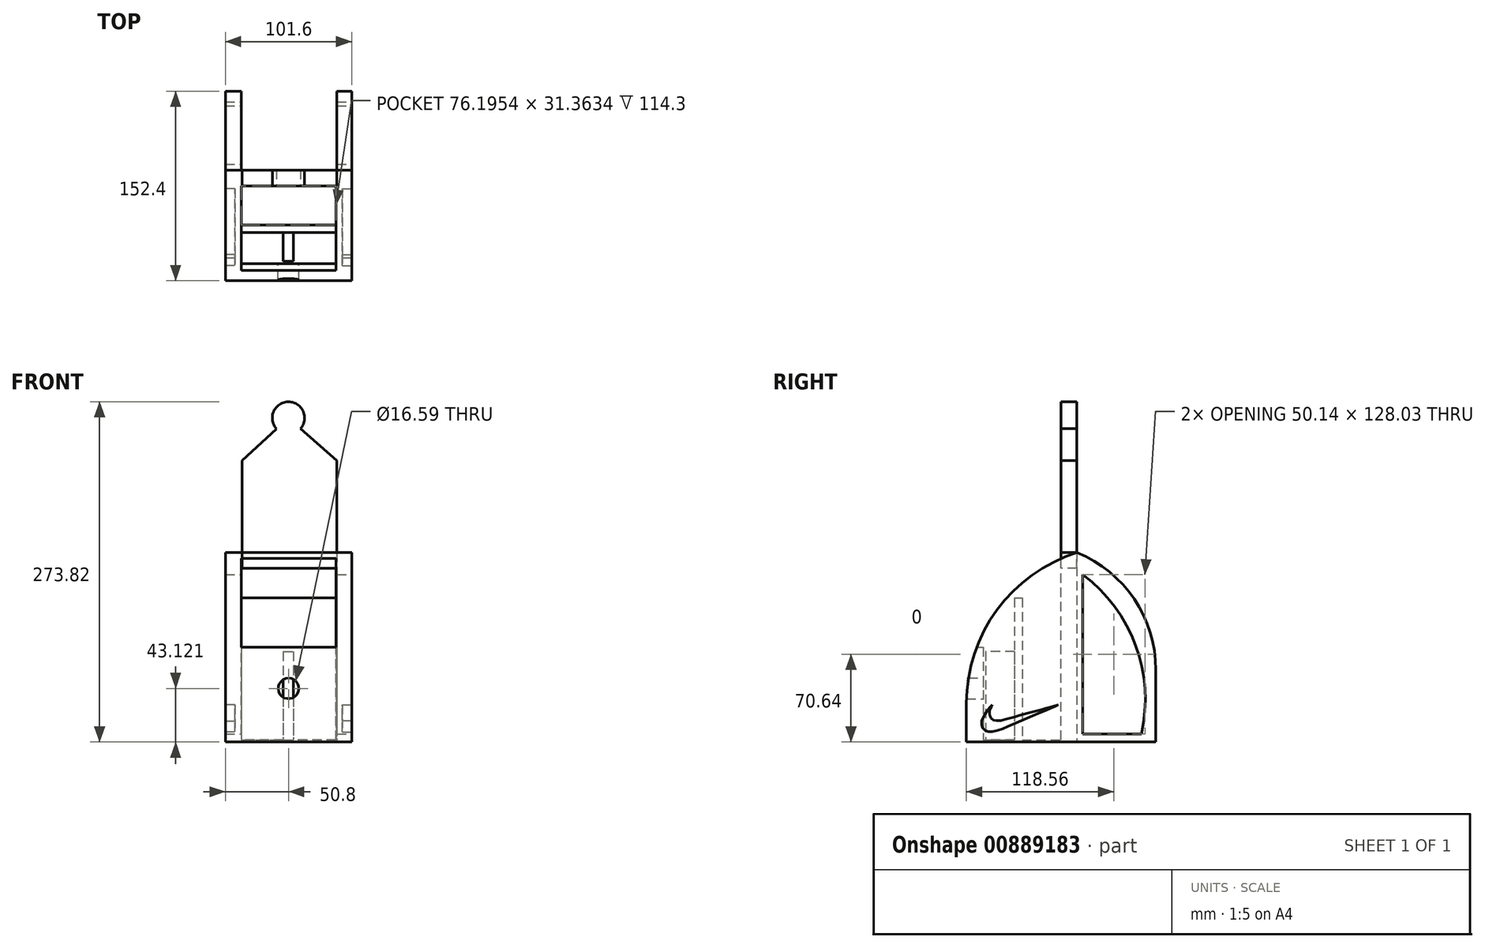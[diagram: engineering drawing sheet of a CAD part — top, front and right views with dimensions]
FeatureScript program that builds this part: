
annotation { "Feature Type Name" : "Feature", "Feature Type Description" : "" }
export const myFeature = defineFeature(function(context is Context, id is Id, definition is map)
    precondition{}
    {
        {
            var Q0;
            Q0=qCreatedBy(makeId("Front.planeOp"),FACE);
            var sketch = newSketch(context, id + "F0", { "sketchPlane" : qUnion([Q0])});
            skLineSegment(sketch, "E0.bottom", {"start": v(50.8, 76.2) * mm, "end": v(-50.8, 76.2) * mm});
            skLineSegment(sketch, "E0.top", {"start": v(50.8, -76.2) * mm, "end": v(-50.8, -76.2) * mm});
            skLineSegment(sketch, "E0.left", {"start": v(50.8, 76.2) * mm, "end": v(50.8, -76.2) * mm});
            skLineSegment(sketch, "E0.right", {"start": v(-50.8, 76.2) * mm, "end": v(-50.8, -76.2) * mm});
            skPoint(sketch, "E0.middle", {"position": v(0, 0) * mm});
            skSolve(sketch);
        }
        {
            var Q0;
            Q0=makeQuery(id+"F0.imprint","IMPRINT",FACE,{"disambiguationData":[TD([[makeQuery(id+"F0.imprint","IMPRINT",EDGE,{"derivedFrom":sQuery(id+"F0.wireOp",EDGE,"E0.bottom")}),1.0]])]});
            extrude(context, id + "F1", {"entities" : qUnion([Q0]), "oppositeDirection" : true, "depth" : 12.7 * mm, "offsetDistance" : 25.4 * mm});
        }
        {
            var Q0;
            Q0=makeQuery(id+"F1.opExtrude","CAP_FACE",FACE,{"disambiguationData":[OSD([sQuery(id+"F0.wireOp",EDGE,"E0.bottom"),sQuery(id+"F0.wireOp",EDGE,"E0.top"),sQuery(id+"F0.wireOp",EDGE,"E0.left"),sQuery(id+"F0.wireOp",EDGE,"E0.right")])],"isStart":true});
            var sketch = newSketch(context, id + "F2", { "sketchPlane" : qUnion([Q0])});
            skLineSegment(sketch, "E1.bottom", {"start": v(-50.8, -76.2) * mm, "end": v(-38.1, -76.2) * mm});
            skLineSegment(sketch, "E1.top", {"start": v(-50.8, -63.5) * mm, "end": v(-38.1, -63.5) * mm});
            skLineSegment(sketch, "E1.left", {"start": v(-50.8, -76.2) * mm, "end": v(-50.8, -63.5) * mm});
            skLineSegment(sketch, "E1.right", {"start": v(-38.1, -76.2) * mm, "end": v(-38.1, -63.5) * mm});
            skLineSegment(sketch, "E2.bottom", {"start": v(50.8, -76.2) * mm, "end": v(38.1, -76.2) * mm});
            skLineSegment(sketch, "E2.top", {"start": v(50.8, -63.5) * mm, "end": v(38.1, -63.5) * mm});
            skLineSegment(sketch, "E2.left", {"start": v(50.8, -76.2) * mm, "end": v(50.8, -63.5) * mm});
            skLineSegment(sketch, "E2.right", {"start": v(38.1, -76.2) * mm, "end": v(38.1, -63.5) * mm});
            skSolve(sketch);
        }
        {
            var Q0;
            Q0=makeQuery(id+"F2.imprint","IMPRINT",FACE,{"disambiguationData":[TD([[makeQuery(id+"F2.imprint","IMPRINT",EDGE,{"derivedFrom":sQuery(id+"F2.wireOp",EDGE,"E1.bottom")}),-1.0]])]});
            var Q1;
            Q1=makeQuery(id+"F2.imprint","IMPRINT",FACE,{"disambiguationData":[TD([[makeQuery(id+"F2.imprint","IMPRINT",EDGE,{"derivedFrom":sQuery(id+"F2.wireOp",EDGE,"E2.bottom")}),-1.0]])]});
            extrude(context, id + "F3", {"entities" : qUnion([Q0, Q1]), "operationType" : NewBodyOperationType.ADD, "depth" : 76.2 * mm, "offsetDistance" : 25.4 * mm});
        }
        {
            var Q0;
            Q0=makeQuery(id+"F1.opExtrude","CAP_FACE",FACE,{"disambiguationData":[OSD([sQuery(id+"F0.wireOp",EDGE,"E0.bottom"),sQuery(id+"F0.wireOp",EDGE,"E0.top"),sQuery(id+"F0.wireOp",EDGE,"E0.left"),sQuery(id+"F0.wireOp",EDGE,"E0.right")])],"isStart":true});
            var sketch = newSketch(context, id + "F4", { "sketchPlane" : qUnion([Q0])});
            skLineSegment(sketch, "E3.bottom", {"start": v(50.8, 76.2) * mm, "end": v(38.1, 76.2) * mm});
            skLineSegment(sketch, "E3.top", {"start": v(50.8, -63.5) * mm, "end": v(38.1, -63.5) * mm});
            skLineSegment(sketch, "E3.left", {"start": v(50.8, 76.2) * mm, "end": v(50.8, -63.5) * mm});
            skLineSegment(sketch, "E3.right", {"start": v(38.1, 76.2) * mm, "end": v(38.1, -63.5) * mm});
            skSolve(sketch);
        }
        {
            var Q0;
            Q0=makeQuery(id+"F1.opExtrude","CAP_FACE",FACE,{"disambiguationData":[OSD([sQuery(id+"F0.wireOp",EDGE,"E0.bottom"),sQuery(id+"F0.wireOp",EDGE,"E0.top"),sQuery(id+"F0.wireOp",EDGE,"E0.left"),sQuery(id+"F0.wireOp",EDGE,"E0.right")])],"isStart":true});
            var sketch = newSketch(context, id + "F5", { "sketchPlane" : qUnion([Q0])});
            skLineSegment(sketch, "E4.bottom", {"start": v(-50.8, 76.2) * mm, "end": v(-38.1, 76.2) * mm});
            skLineSegment(sketch, "E4.top", {"start": v(-50.8, -63.5) * mm, "end": v(-38.1, -63.5) * mm});
            skLineSegment(sketch, "E4.left", {"start": v(-50.8, 76.2) * mm, "end": v(-50.8, -63.5) * mm});
            skLineSegment(sketch, "E4.right", {"start": v(-38.1, 76.2) * mm, "end": v(-38.1, -63.5) * mm});
            skSolve(sketch);
        }
        {
            var Q0;
            Q0 = qSketchRegion(id + "F4", true);
            var Q1;
            Q1 = qSketchRegion(id + "F5", true);
            extrude(context, id + "F6", {"entities" : qUnion([Q0, Q1]), "operationType" : NewBodyOperationType.ADD, "depth" : 76.2 * mm, "offsetDistance" : 25.4 * mm});
        }
        {
            var Q0;
            Q0=makeQuery(id+"F6.opExtrude","CAP_EDGE",EDGE,{"disambiguationData":[OSD([sQuery(id+"F5.wireOp",EDGE,"E4.bottom")])],"isStart":false});
            var Q1;
            Q1=makeQuery(id+"F6.opExtrude","CAP_EDGE",EDGE,{"disambiguationData":[OSD([sQuery(id+"F4.wireOp",EDGE,"E3.bottom")])],"isStart":false});
            fillet(context, id + "F7", {"entities" : qUnion([Q0, Q1]), "radius" : 127 * mm, "tangentPropagation" : true, "allowEdgeOverflow" : false});
        }
        {
            var Q0;
            Q0=makeQuery(id+"F6.boolean.opBoolean","MERGE",FACE,{"derivedFrom":[makeQuery(id+"F3.opExtrude","SWEPT_FACE",FACE,{"disambiguationData":[OSD([sQuery(id+"F2.wireOp",EDGE,"E1.right")])]}),makeQuery(id+"F6.opExtrude","SWEPT_FACE",FACE,{"disambiguationData":[OSD([sQuery(id+"F5.wireOp",EDGE,"E4.right")])]})]});
            var sketch = newSketch(context, id + "F8", { "sketchPlane" : qUnion([Q0])});
            skLineSegment(sketch, "E5.bottom", {"start": v(-76.2, -76.2) * mm, "end": v(-62.73, -76.2) * mm});
            skLineSegment(sketch, "E5.top", {"start": v(-76.2, 0) * mm, "end": v(-62.73, 0) * mm});
            skLineSegment(sketch, "E5.left", {"start": v(-76.2, -76.2) * mm, "end": v(-76.2, 0) * mm});
            skLineSegment(sketch, "E6", {"start": v(-62.73, 0) * mm, "end": v(-62.73, -76.2) * mm});
            skPoint(sketch, "E5.right.end.orphan", {"position": v(-49.25, 0) * mm});
            skPoint(sketch, "E7.orphan", {"position": v(-49.25, -76.2) * mm});
            skSolve(sketch);
        }
        {
            var Q0;
            {var subQ1=sQuery(id+"F8.wireOp",EDGE,"E5.bottom");Q0=makeQuery(id+"F8.imprint","IMPRINT",FACE,{"disambiguationData":[TD([[makeQuery(id+"F8.imprint","IMPRINT",EDGE,{"derivedFrom":subQ1}),1.0]])]});}
            extrude(context, id + "F9", {"entities" : qUnion([Q0]), "operationType" : NewBodyOperationType.ADD, "depth" : 88.9 * mm, "offsetDistance" : 25.4 * mm});
        }
        {
            var Q0;
            Q0=makeQuery(id+"F6.boolean.opBoolean","MERGE",FACE,{"derivedFrom":[makeQuery(id+"F3.opExtrude","SWEPT_FACE",FACE,{"disambiguationData":[OSD([sQuery(id+"F2.wireOp",EDGE,"E2.right")])]}),makeQuery(id+"F6.opExtrude","SWEPT_FACE",FACE,{"disambiguationData":[OSD([sQuery(id+"F4.wireOp",EDGE,"E3.right")])]})]});
            var sketch = newSketch(context, id + "F10", { "sketchPlane" : qUnion([Q0])});
            skLineSegment(sketch, "E8.bottom", {"start": v(0, -74.52) * mm, "end": v(62.73, -74.52) * mm});
            skLineSegment(sketch, "E8.top", {"start": v(0, -76.2) * mm, "end": v(62.73, -76.2) * mm});
            skLineSegment(sketch, "E8.left", {"start": v(0, -74.52) * mm, "end": v(0, -76.2) * mm});
            skLineSegment(sketch, "E8.right", {"start": v(62.73, -74.52) * mm, "end": v(62.73, -76.2) * mm});
            skSolve(sketch);
        }
        {
            var Q0;
            Q0=makeQuery(id+"F10.imprint","IMPRINT",FACE,{"disambiguationData":[TD([[makeQuery(id+"F10.imprint","IMPRINT",EDGE,{"derivedFrom":sQuery(id+"F10.wireOp",EDGE,"E8.bottom")}),-1.0]])]});
            extrude(context, id + "F11", {"entities" : qUnion([Q0]), "operationType" : NewBodyOperationType.ADD, "depth" : 88.9 * mm, "offsetDistance" : 25.4 * mm});
        }
        {
            var Q0;
            Q0=makeQuery(id+"F9.opExtrude","SWEPT_FACE",FACE,{"disambiguationData":[OSD([sQuery(id+"F8.wireOp",EDGE,"E6")])]});
            var sketch = newSketch(context, id + "F12", { "sketchPlane" : qUnion([Q0])});
            skCircle(sketch, "E9", {"center": v(0, -33.08) * mm, "radius": 8.3 * mm});
            skSolve(sketch);
        }
        {
            var Q0;
            Q0 = qSketchRegion(id + "F12", true);
            extrude(context, id + "F13", {"entities" : qUnion([Q0]), "operationType" : NewBodyOperationType.REMOVE, "oppositeDirection" : true, "depth" : 25.4 * mm, "offsetDistance" : 25.4 * mm});
        }
        {
            var Q0;
            Q0=makeQuery(id+"F0.imprint","IMPRINT",FACE,{"disambiguationData":[TD([[makeQuery(id+"F0.imprint","IMPRINT",EDGE,{"derivedFrom":sQuery(id+"F0.wireOp",EDGE,"E0.bottom")}),1.0]])]});
            var sketch = newSketch(context, id + "F14", { "sketchPlane" : qUnion([Q0])});
            skLineSegment(sketch, "E10", {"start": v(-37.42, 74.01) * mm, "end": v(36.32, 74.01) * mm});
            skLineSegment(sketch, "E11.bottom", {"start": v(-37.42, 74.01) * mm, "end": v(38.78, 74.01) * mm});
            skLineSegment(sketch, "E11.left", {"start": v(-37.42, 74.01) * mm, "end": v(-37.42, 150.21) * mm});
            skLineSegment(sketch, "E11.right", {"start": v(38.78, 74.01) * mm, "end": v(38.78, 150.21) * mm});
            skLineSegment(sketch, "E12", {"start": v(-37.42, 150.21) * mm, "end": v(-9.6, 175.8) * mm});
            skLineSegment(sketch, "E13", {"start": v(9.7, 175.99) * mm, "end": v(38.78, 150.21) * mm});
            skPoint(sketch, "E14.orphan", {"position": v(0, 192.46) * mm});
            skPoint(sketch, "E15.start.orphan", {"position": v(-0.55, 74.01) * mm});
            skArc(sketch, "E16", {"start": v(9.7, 175.99) * mm, "mid": v(-0.16, 197.62) * mm, "end": v(-9.6, 175.8) * mm});
            skSolve(sketch);
        }
        {
            var Q0;
            {var subQ1=sQuery(id+"F14.wireOp",EDGE,"E12");Q0=makeQuery(id+"F14.imprint","IMPRINT",FACE,{"disambiguationData":[TD([[makeQuery(id+"F14.imprint","IMPRINT",EDGE,{"derivedFrom":subQ1}),-1.0]])]});}
            extrude(context, id + "F15", {"entities" : qUnion([Q0]), "oppositeDirection" : true, "depth" : 12.7 * mm, "offsetDistance" : 25.4 * mm});
        }
        {
            var Q0;
            Q0=makeQuery(id+"F15.opExtrude","SWEPT_FACE",FACE,{"disambiguationData":[OSD([sQuery(id+"F0.wireOp",EDGE,"E0.bottom")])]});
            extrude(context, id + "F16", {"entities" : qUnion([Q0]), "depth" : 12.7 * mm, "offsetDistance" : 25.4 * mm});
        }
        {
            var Q0;
            Q0=makeQuery(id+"F11.opExtrude","SWEPT_FACE",FACE,{"disambiguationData":[OSD([sQuery(id+"F10.wireOp",EDGE,"E8.bottom")])]});
            var sketch = newSketch(context, id + "F17", { "sketchPlane" : qUnion([Q0])});
            skLineSegment(sketch, "E17.bottom", {"start": v(38.1, -31.36) * mm, "end": v(-38.1, -31.36) * mm});
            skLineSegment(sketch, "E17.top", {"start": v(38.1, -37.5) * mm, "end": v(3.89, -37.5) * mm});
            skLineSegment(sketch, "E17.left", {"start": v(38.1, -31.36) * mm, "end": v(38.1, -37.5) * mm});
            skLineSegment(sketch, "E17.right", {"start": v(-38.1, -31.36) * mm, "end": v(-38.1, -37.5) * mm});
            skPoint(sketch, "E17.middle", {"position": v(0, -34.43) * mm});
            skLineSegment(sketch, "E18", {"start": v(-4.17, -37.5) * mm, "end": v(-4.17, -60.7) * mm});
            skLineSegment(sketch, "E19", {"start": v(3.89, -37.5) * mm, "end": v(3.89, -60.7) * mm});
            skLineSegment(sketch, "E20.trimOffspring", {"start": v(-4.17, -37.5) * mm, "end": v(-38.1, -37.5) * mm});
            skLineSegment(sketch, "E21", {"start": v(-4.17, -37.5) * mm, "end": v(3.89, -37.5) * mm});
            skLineSegment(sketch, "E22", {"start": v(-4.17, -60.7) * mm, "end": v(3.89, -60.7) * mm});
            skSolve(sketch);
        }
        {
            var Q0;
            Q0=makeQuery(id+"F17.imprint","IMPRINT",FACE,{"disambiguationData":[TD([[makeQuery(id+"F17.imprint","IMPRINT",EDGE,{"derivedFrom":sQuery(id+"F17.wireOp",EDGE,"E17.bottom")}),1.0]])]});
            extrude(context, id + "F18", {"entities" : qUnion([Q0]), "operationType" : NewBodyOperationType.ADD, "depth" : 114.3 * mm, "offsetDistance" : 25.4 * mm});
        }
        {
            var Q0;
            {var subQ0=sQuery(id+"F17.wireOp",EDGE,"E21");Q0=makeQuery(id+"F17.imprint","IMPRINT",FACE,{"disambiguationData":[TD([[makeQuery(id+"F17.imprint","IMPRINT",EDGE,{"derivedFrom":subQ0}),-1.0]])]});}
            extrude(context, id + "F19", {"entities" : qUnion([Q0]), "operationType" : NewBodyOperationType.ADD, "depth" : 71.12 * mm, "offsetDistance" : 25.4 * mm});
        }
        {
            var Q0;
            Q0=makeQuery(id+"F6.boolean.opBoolean","MERGE",FACE,{"derivedFrom":[makeQuery(id+"F3.boolean.opBoolean","MERGE",FACE,{"derivedFrom":[makeQuery(id+"F1.opExtrude","SWEPT_FACE",FACE,{"disambiguationData":[OSD([sQuery(id+"F0.wireOp",EDGE,"E0.left")])]}),makeQuery(id+"F3.opExtrude","SWEPT_FACE",FACE,{"disambiguationData":[OSD([sQuery(id+"F2.wireOp",EDGE,"E2.left")])]})]}),makeQuery(id+"F6.opExtrude","SWEPT_FACE",FACE,{"disambiguationData":[OSD([sQuery(id+"F4.wireOp",EDGE,"E3.left")])]})]});
            var sketch = newSketch(context, id + "F20", { "sketchPlane" : qUnion([Q0])});
            skFitSpline(sketch, "E23", {"points": [v(-2.36, -46.39) * mm, v(-10.34, -48.62) * mm, v(-14.44, -49.72) * mm, v(-22.05, -51.74) * mm, v(-29.62, -53.78) * mm, v(-37.23, -55.83) * mm, v(-45.46, -58.02) * mm, v(-49.16, -58.95) * mm, v(-49.48, -58.95) * mm, v(-52.92, -58.93) * mm, v(-55.53, -57.88) * mm, v(-57.2, -55.72) * mm, v(-57.74, -53.24) * mm, v(-57.5, -51.11) * mm, v(-56.78, -48.9) * mm, v(-55.84, -47.12) * mm, v(-55.26, -46.1) * mm], "startDerivative": vector(-95.07, -26.72) * mm, "endDerivative": vector(15.46, 27.49) * mm});
            skFitSpline(sketch, "E24", {"points": [v(-55.26, -46.1) * mm, v(-56.78, -47.75) * mm, v(-58.9, -50.27) * mm, v(-60.65, -52.67) * mm, v(-62.18, -55.14) * mm, v(-63.53, -58.25) * mm, v(-63.96, -60.53) * mm, v(-64, -62.88) * mm, v(-63.36, -64.75) * mm, v(-61.37, -66.83) * mm, v(-59.2, -67.74) * mm, v(-56.79, -67.98) * mm, v(-52.66, -67.4) * mm, v(-47.68, -65.72) * mm, v(-41.9, -63.25) * mm, v(-35.59, -60.49) * mm, v(-29.33, -57.9) * mm, v(-23.78, -55.43) * mm, v(-17.24, -52.7) * mm, v(-11.97, -50.44) * mm, v(-8.06, -48.76) * mm, v(-3.66, -47.07) * mm, v(-2.36, -46.39) * mm], "startDerivative": vector(-41.61, -44.2) * mm, "endDerivative": vector(37.56, 22.42) * mm});
            skSolve(sketch);
        }
        {
            var Q0;
            Q0=makeQuery(id+"F20.imprint","IMPRINT",FACE,{"disambiguationData":[TD([[makeQuery(id+"F20.imprint","IMPRINT",EDGE,{"derivedFrom":sQuery(id+"F20.wireOp",EDGE,"E23")}),1.0]])]});
            extrude(context, id + "F21", {"entities" : qUnion([Q0]), "operationType" : NewBodyOperationType.REMOVE, "oppositeDirection" : true, "depth" : 7.62 * mm, "offsetDistance" : 25.4 * mm});
        }
        {
            var Q0;
            Q0=makeQuery(id+"F6.boolean.opBoolean","MERGE",FACE,{"derivedFrom":[makeQuery(id+"F3.boolean.opBoolean","MERGE",FACE,{"derivedFrom":[makeQuery(id+"F1.opExtrude","SWEPT_FACE",FACE,{"disambiguationData":[OSD([sQuery(id+"F0.wireOp",EDGE,"E0.right")])]}),makeQuery(id+"F3.opExtrude","SWEPT_FACE",FACE,{"disambiguationData":[OSD([sQuery(id+"F2.wireOp",EDGE,"E1.left")])]})]}),makeQuery(id+"F6.opExtrude","SWEPT_FACE",FACE,{"disambiguationData":[OSD([sQuery(id+"F5.wireOp",EDGE,"E4.left")])]})]});
            var sketch = newSketch(context, id + "F22", { "sketchPlane" : qUnion([Q0])});
            skFitSpline(sketch, "E25", {"points": [v(2.36, -46.39) * mm, v(10.34, -48.62) * mm, v(15.14, -49.93) * mm, v(20.14, -51.26) * mm, v(26.05, -52.88) * mm, v(33.77, -54.97) * mm, v(43.51, -57.53) * mm, v(49.17, -58.96) * mm, v(52.95, -58.96) * mm, v(55.51, -57.95) * mm, v(56.95, -56.43) * mm, v(57.66, -54.65) * mm, v(57.75, -52.35) * mm, v(57.06, -49.61) * mm, v(55.86, -47.11) * mm, v(55.27, -46.09) * mm], "startDerivative": vector(90.7, -25.45) * mm, "endDerivative": vector(-15.1, 25.44) * mm});
            skFitSpline(sketch, "E26", {"points": [v(55.27, -46.09) * mm, v(56.4, -47.36) * mm, v(57.72, -48.88) * mm, v(59.1, -50.56) * mm, v(61.6, -54.14) * mm, v(63.17, -57.3) * mm, v(63.84, -59.62) * mm, v(63.92, -60.39) * mm, v(63.96, -62.76) * mm, v(62.98, -65.3) * mm, v(61.21, -66.93) * mm, v(58.69, -67.8) * mm, v(55.4, -67.89) * mm, v(50.81, -66.81) * mm, v(47.32, -65.51) * mm, v(42.99, -63.7) * mm, v(36.39, -60.81) * mm, v(30.23, -58.24) * mm, v(22.8, -55) * mm, v(15.47, -51.93) * mm, v(8.3, -48.84) * mm, v(3.5, -46.92) * mm, v(2.36, -46.39) * mm], "startDerivative": vector(35.36, -39.87) * mm, "endDerivative": vector(-35.27, 17.7) * mm});
            skSolve(sketch);
        }
        {
            var Q0;
            Q0=makeQuery(id+"F22.imprint","IMPRINT",FACE,{"disambiguationData":[TD([[makeQuery(id+"F22.imprint","IMPRINT",EDGE,{"derivedFrom":sQuery(id+"F22.wireOp",EDGE,"E25")}),-1.0]])]});
            extrude(context, id + "F23", {"entities" : qUnion([Q0]), "operationType" : NewBodyOperationType.REMOVE, "oppositeDirection" : true, "depth" : 7.62 * mm, "offsetDistance" : 25.4 * mm});
        }
        {
            var Q0;
            Q0=makeQuery(id+"F1.opExtrude","CAP_FACE",FACE,{"disambiguationData":[OSD([sQuery(id+"F0.wireOp",EDGE,"E0.bottom"),sQuery(id+"F0.wireOp",EDGE,"E0.top"),sQuery(id+"F0.wireOp",EDGE,"E0.left"),sQuery(id+"F0.wireOp",EDGE,"E0.right")])],"isStart":false});
            var sketch = newSketch(context, id + "F24", { "sketchPlane" : qUnion([Q0])});
            skLineSegment(sketch, "E27.bottom", {"start": v(-50.8, 76.2) * mm, "end": v(-38.9, 76.2) * mm});
            skLineSegment(sketch, "E27.top", {"start": v(-50.8, -76.2) * mm, "end": v(-38.9, -76.2) * mm});
            skLineSegment(sketch, "E27.left", {"start": v(-50.8, 76.2) * mm, "end": v(-50.8, -76.2) * mm});
            skLineSegment(sketch, "E27.right", {"start": v(-38.9, 76.2) * mm, "end": v(-38.9, -76.2) * mm});
            skLineSegment(sketch, "E28.bottom", {"start": v(50.8, 76.2) * mm, "end": v(38.09, 76.2) * mm});
            skLineSegment(sketch, "E28.top", {"start": v(50.8, -76.2) * mm, "end": v(38.09, -76.2) * mm});
            skLineSegment(sketch, "E28.left", {"start": v(50.8, 76.2) * mm, "end": v(50.8, -76.2) * mm});
            skLineSegment(sketch, "E28.right", {"start": v(38.09, 76.2) * mm, "end": v(38.09, -76.2) * mm});
            skSolve(sketch);
        }
        {
            var Q0;
            Q0=makeQuery(id+"F24.imprint","IMPRINT",FACE,{"disambiguationData":[TD([[makeQuery(id+"F24.imprint","IMPRINT",EDGE,{"derivedFrom":sQuery(id+"F24.wireOp",EDGE,"E27.bottom")}),-1.0]])]});
            var Q1;
            Q1=makeQuery(id+"F24.imprint","IMPRINT",FACE,{"disambiguationData":[TD([[makeQuery(id+"F24.imprint","IMPRINT",EDGE,{"derivedFrom":sQuery(id+"F24.wireOp",EDGE,"E28.bottom")}),-1.0]])]});
            extrude(context, id + "F25", {"entities" : qUnion([Q0, Q1]), "operationType" : NewBodyOperationType.ADD, "depth" : 63.5 * mm, "offsetDistance" : 25.4 * mm});
        }
        {
            var Q0;
            Q0=makeQuery(id+"F25.opExtrude","CAP_EDGE",EDGE,{"disambiguationData":[OSD([sQuery(id+"F24.wireOp",EDGE,"E27.bottom")])],"isStart":false});
            var Q1;
            Q1=makeQuery(id+"F25.opExtrude","CAP_EDGE",EDGE,{"disambiguationData":[OSD([sQuery(id+"F24.wireOp",EDGE,"E28.bottom")])],"isStart":false});
            fillet(context, id + "F26", {"entities" : qUnion([Q0, Q1]), "radius" : 101.6 * mm, "tangentPropagation" : true, "allowEdgeOverflow" : false});
        }
        {
            var Q0;
            Q0=makeQuery(id+"F25.boolean.opBoolean","MERGE",FACE,{"derivedFrom":[makeQuery(id+"F6.boolean.opBoolean","MERGE",FACE,{"derivedFrom":[makeQuery(id+"F3.boolean.opBoolean","MERGE",FACE,{"derivedFrom":[makeQuery(id+"F1.opExtrude","SWEPT_FACE",FACE,{"disambiguationData":[OSD([sQuery(id+"F0.wireOp",EDGE,"E0.left")])]}),makeQuery(id+"F3.opExtrude","SWEPT_FACE",FACE,{"disambiguationData":[OSD([sQuery(id+"F2.wireOp",EDGE,"E2.left")])]})]}),makeQuery(id+"F6.opExtrude","SWEPT_FACE",FACE,{"disambiguationData":[OSD([sQuery(id+"F4.wireOp",EDGE,"E3.left")])]})]}),makeQuery(id+"F25.opExtrude","SWEPT_FACE",FACE,{"disambiguationData":[OSD([sQuery(id+"F24.wireOp",EDGE,"E27.left")])]})]});
            var sketch = newSketch(context, id + "F27", { "sketchPlane" : qUnion([Q0])});
            skLineSegment(sketch, "E29", {"start": v(17.29, 58.46) * mm, "end": v(17.29, -69.58) * mm});
            skLineSegment(sketch, "E30", {"start": v(17.29, -69.58) * mm, "end": v(64.53, -69.58) * mm});
            skArc(sketch, "E31", {"start": v(64.53, -69.58) * mm, "mid": v(59.98, 1.48) * mm, "end": v(17.29, 58.46) * mm});
            skSolve(sketch);
        }
        {
            var Q0;
            Q0=makeQuery(id+"F27.imprint","IMPRINT",FACE,{"disambiguationData":[TD([[makeQuery(id+"F27.imprint","IMPRINT",EDGE,{"derivedFrom":sQuery(id+"F27.wireOp",EDGE,"E29")}),1.0]])]});
            extrude(context, id + "F28", {"entities" : qUnion([Q0]), "operationType" : NewBodyOperationType.REMOVE, "oppositeDirection" : true, "depth" : 152.4 * mm, "offsetDistance" : 25.4 * mm});
        }
    });
